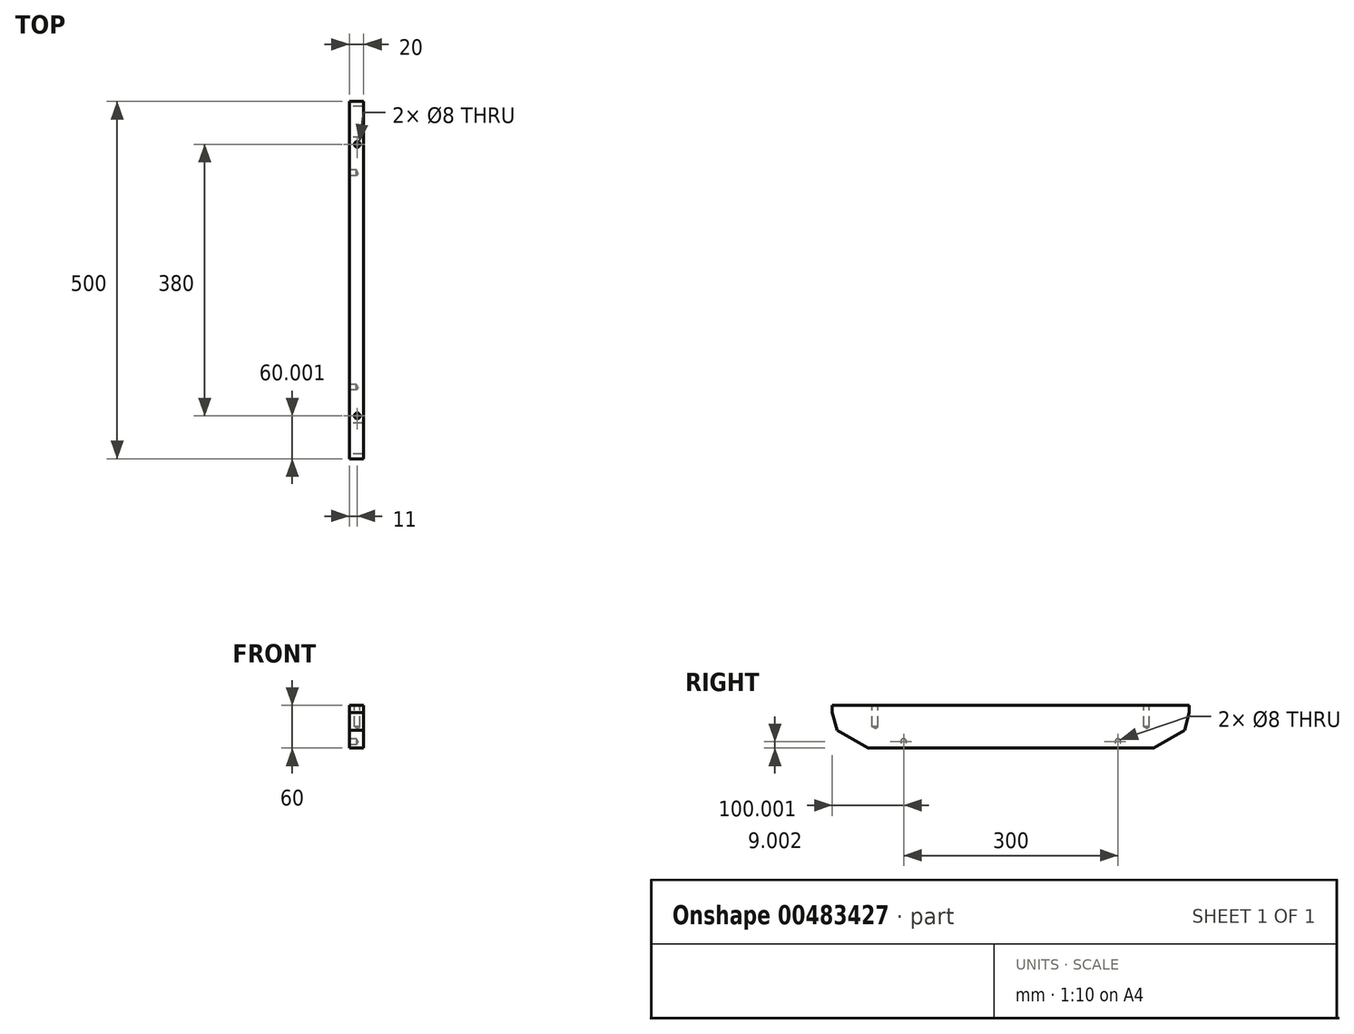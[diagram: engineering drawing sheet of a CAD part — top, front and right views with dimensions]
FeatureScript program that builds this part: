
annotation { "Feature Type Name" : "Feature", "Feature Type Description" : "" }
export const myFeature = defineFeature(function(context is Context, id is Id, definition is map)
    precondition{}
    {
        {
            var Q0;
            Q0=qCreatedBy(makeId("Right.planeOp"),FACE);
            var sketch = newSketch(context, id + "F0", { "sketchPlane" : qUnion([Q0])});
            skLineSegment(sketch, "E0.top", {"start": v(246.88, 40.02) * mm, "end": v(-253.12, 40.02) * mm});
            skLineSegment(sketch, "E1", {"start": v(-253.12, 40.02) * mm, "end": v(-253.12, 30.02) * mm});
            skLineSegment(sketch, "E2", {"start": v(-253.12, 30.02) * mm, "end": v(-246.42, 5.02) * mm});
            skLineSegment(sketch, "E3", {"start": v(-246.42, 5.02) * mm, "end": v(-203.12, -19.98) * mm});
            skLineSegment(sketch, "E4", {"start": v(-203.12, -19.98) * mm, "end": v(196.88, -19.98) * mm});
            skLineSegment(sketch, "E5", {"start": v(196.88, -19.98) * mm, "end": v(240.18, 5.02) * mm});
            skLineSegment(sketch, "E6", {"start": v(240.18, 5.02) * mm, "end": v(246.88, 30.02) * mm});
            skLineSegment(sketch, "E7", {"start": v(246.88, 30.02) * mm, "end": v(246.88, 40.02) * mm});
            skSolve(sketch);
        }
        {
            var Q0;
            Q0=qSketchRegion(id+"F0",true);
            extrude(context, id + "F1", {"entities" : qUnion([Q0]), "depth" : 20 * mm});
        }
        {
            var Q0;
            Q0=makeQuery(id+"F1.opExtrude","SWEPT_FACE",FACE,{"disambiguationData":[OSD([sQuery(id+"F0.wireOp",EDGE,"E0.top")])]});
            var sketch = newSketch(context, id + "F2", { "sketchPlane" : qUnion([Q0])});
            skPoint(sketch, "E8", {"position": v(11, -193.12) * mm});
            skPoint(sketch, "E9", {"position": v(11, 186.88) * mm});
            skSolve(sketch);
        }
        {
            var Q0;
            Q0=makeQuery(id+"F1.opExtrude","CAP_FACE",FACE,{"disambiguationData":[OSD([sQuery(id+"F0.wireOp",EDGE,"E0.top"),sQuery(id+"F0.wireOp",EDGE,"E1"),sQuery(id+"F0.wireOp",EDGE,"E2"),sQuery(id+"F0.wireOp",EDGE,"E3"),sQuery(id+"F0.wireOp",EDGE,"E4"),sQuery(id+"F0.wireOp",EDGE,"E5"),sQuery(id+"F0.wireOp",EDGE,"E6"),sQuery(id+"F0.wireOp",EDGE,"E7")])],"isStart":true});
            var sketch = newSketch(context, id + "F3", { "sketchPlane" : qUnion([Q0])});
            skPoint(sketch, "E10", {"position": v(-146.88, -10.98) * mm});
            skPoint(sketch, "E11", {"position": v(153.12, -10.98) * mm});
            skSolve(sketch);
        }
        {
            var Q0;
            Q0=sQuery(id+"F2.wireOp",VERTEX,"E9");
            var Q1;
            Q1=sQuery(id+"F2.wireOp",VERTEX,"E8");
            var Q2;
            Q2=makeQuery(id+"F1.opExtrude","SWEPT_BODY",BODY,{"disambiguationData":[OSD([sQuery(id+"F0.wireOp",EDGE,"E0.top"),sQuery(id+"F0.wireOp",EDGE,"E1"),sQuery(id+"F0.wireOp",EDGE,"E2"),sQuery(id+"F0.wireOp",EDGE,"E3"),sQuery(id+"F0.wireOp",EDGE,"E4"),sQuery(id+"F0.wireOp",EDGE,"E5"),sQuery(id+"F0.wireOp",EDGE,"E6"),sQuery(id+"F0.wireOp",EDGE,"E7")])]});
            hole(context, id + "F4", {"style" : HoleStyle.SIMPLE, "endStyle" : HoleEndStyle.BLIND, "standardTappedOrClearance" : lookupTablePath({ "standard" : "ISO", "size" : "8", "type" : "Drilled" }), "standardBlindInLast" : lookupTablePath({ "standard" : "ISO", "size" : "8", "type" : "Drilled" }), "holeDiameter" : 8 * mm, "holeDepth" : 30 * mm, "isTappedThrough" : true, "tappedDepth" : 12 * mm, "tapClearance" : 3, "locations" : qUnion([Q0, Q1]), "scope" : qUnion([Q2])});
        }
        {
            var Q0;
            Q0=sQuery(id+"F3.wireOp",VERTEX,"E11");
            var Q1;
            Q1=sQuery(id+"F3.wireOp",VERTEX,"E10");
            var Q2;
            Q2=makeQuery(id+"F1.opExtrude","SWEPT_BODY",BODY,{"disambiguationData":[OSD([sQuery(id+"F0.wireOp",EDGE,"E0.top"),sQuery(id+"F0.wireOp",EDGE,"E1"),sQuery(id+"F0.wireOp",EDGE,"E2"),sQuery(id+"F0.wireOp",EDGE,"E3"),sQuery(id+"F0.wireOp",EDGE,"E4"),sQuery(id+"F0.wireOp",EDGE,"E5"),sQuery(id+"F0.wireOp",EDGE,"E6"),sQuery(id+"F0.wireOp",EDGE,"E7")])]});
            hole(context, id + "F5", {"style" : HoleStyle.SIMPLE, "endStyle" : HoleEndStyle.BLIND, "standardTappedOrClearance" : lookupTablePath({ "standard" : "ISO", "size" : "8", "type" : "Drilled" }), "standardBlindInLast" : lookupTablePath({ "standard" : "ISO", "size" : "8", "type" : "Drilled" }), "holeDiameter" : 8 * mm, "holeDepth" : 10 * mm, "isTappedThrough" : true, "tappedDepth" : 12 * mm, "tapClearance" : 3, "locations" : qUnion([Q0, Q1]), "scope" : qUnion([Q2])});
        }
    });
